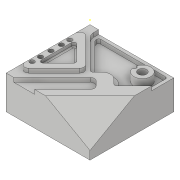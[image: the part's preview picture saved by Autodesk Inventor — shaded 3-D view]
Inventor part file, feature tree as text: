
AUTODESK INVENTOR PART (.ipt)
format: ipt  version: 2018 (Build 220112000, 112)  size: 334,848 bytes
history: native  units: in
note: dims shown in document units (in); Inventor stores cm internally (conversion verified against a paired STEP export)
features: sketch x16, extrude x13, fillet x9, thread x3, hole x2, plane x1
ambient origin geometry x8: Origin, YZ Plane, XZ Plane, XY Plane, X Axis, Y Axis, Z Axis, Center Point
bodies: Solid1 (feature_tree)
feature tree (44):
  extrude  "Extrusion1"  Depth=3.1496in
  extrude  "Extrusion2"  Depth=1.5748in
  plane  "Work Plane1"
  extrude  "Extrusion3"  Depth=0.4331in
  fillet  "Fillet1"  Radius=0.4331in
  sketch  "Sketch5"  dims[d29=0.2756in d30=0.2756in]
  extrude  "Extrusion5"  Depth=0.2756in
  extrude  "Extrusion6"  Depth=0.3937in
  extrude  "Extrusion7"  Depth=7.874in TaperAngle=0.0deg
  fillet  "Fillet2"  Radius=0.1969in
  extrude  "Extrusion8"  Depth=0.3937in TaperAngle=0.0deg
  extrude  "Extrusion9"  Depth=0.7874in
  extrude  "Extrusion10"  Depth=0.3937in TaperAngle=0.0deg
  fillet  "Fillet3"  Radius=0.7874in
  extrude  "Extrusion11"  Depth=0.9843in
  fillet  "Fillet4"  [1 undecoded]
  fillet  "Fillet5"  Radius=0.2953in
  fillet  "Fillet6"  Radius=0.2953in
  extrude  "Extrusion12"  Depth=0.3937in TaperAngle=0.0deg
  fillet  "Fillet7"  [1 undecoded]
  fillet  "Fillet8"  Radius=0.7874in
  extrude  "Extrusion13"  Depth=0.3937in
  extrude  "Extrusion14"  Depth=0.1969in
  fillet  "Fillet9"  Radius=0.1969in
  hole  "Hole1"  [1 undecoded]
  hole  "Hole2"  [1 undecoded]
  thread  "Thread1"  [1 undecoded]
  thread  "Thread2"  [1 undecoded]
  thread  "Thread3"  [1 undecoded]
  sketch  "Sketch1"  dims[d0=7.874in d1=3.1496in]
  sketch  "Sketch2"  dims[d2=7.874in d3=0.0in d20=1.5748in]
  sketch  "Sketch3"  dims[d22=0.4331in d24=0.4331in d26=0.4331in]
  sketch  "Sketch6"  dims[d31=0.3937in d32=0.0in d33=2.9528in]
  sketch  "Sketch7"  dims[d34=2.3622in d35=7.874in d36=0.0in d37=0.1969in]
  sketch  "Sketch8"  dims[d41=0.3937in d42=0.0in d43=0.3937in d44=0.0in]
  sketch  "Sketch9"  dims[d45=0.7874in d46=5.9055in]
  sketch  "Sketch10"  dims[d47=45.0deg d48=0.3937in d49=0.0in d50=0.7874in]
  sketch  "Sketch11"  dims[d51=0.9843in d52=0.9843in d53=45.0deg d54=0.2953in d55=0.2953in]
  sketch  "Sketch12"  dims[d56=0.3937in d57=0.0in d58=0.3937in d59=0.3937in d60=0.0in d61=0.0in d62=135.0deg d63=0.7874in d64=0.0in]
  sketch  "Sketch13"  dims[d65=0.3937in d66=2.1654in]
  sketch  "Sketch14"  dims[d67=0.7874in d68=0.0in d69=0.1969in d70=0.1969in]
  sketch  "Sketch15"  dims[d71=0.1969in d72=1.378in]
  sketch  "Sketch17"  dims[d73=1.5748in d74=1.5748in d75=0.7874in d76=0.7874in d77=0.0in d78=0.3937in]
  sketch  "Sketch18"  dims[d79=0.1181in d80=0.4331in d81=0.7874in d82=0.0in d83=1.378in d84=0.3937in d85=0.0in d86=0.3937in d89=0.4331in d90=0.2362in d91=0.1575in d92=0.0787in d93=90.0deg d94=0.9843in d95=0.8108in d96=0.4331in d97=0.2362in d98=0.1575in d99=0.0787in d100=90.0deg d101=0.9843in d102=0.8108in d103=0.5906in d104=0.0in d105=0.5906in d106=0.0in d107=0.5906in d108=0.0in]
note: 7 required parameter values undecoded (feature->parameter linkage not recoverable at this tier; creation-order binding heuristic only, values carry confidence <= 0.55)
